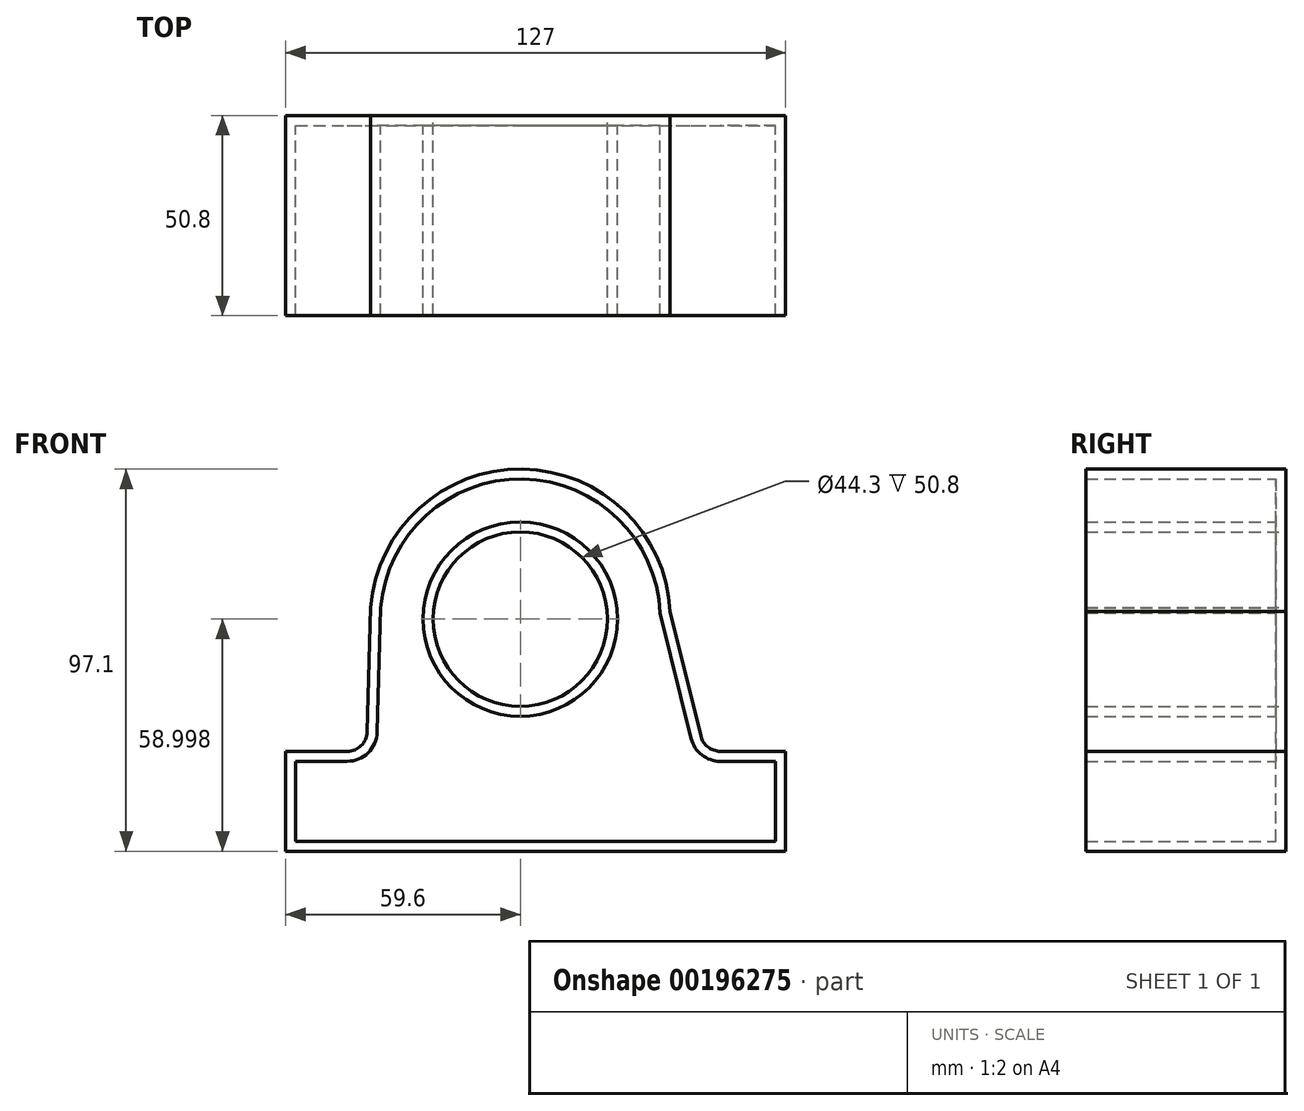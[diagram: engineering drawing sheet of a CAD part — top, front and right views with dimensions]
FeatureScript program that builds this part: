
annotation { "Feature Type Name" : "Feature", "Feature Type Description" : "" }
export const myFeature = defineFeature(function(context is Context, id is Id, definition is map)
    precondition{}
    {
        {
            var Q0;
            Q0=qCreatedBy(makeId("Front.planeOp"),FACE);
            var sketch = newSketch(context, id + "F0", { "sketchPlane" : qUnion([Q0])});
            skLineSegment(sketch, "E0", {"start": v(-59.6, -39.48) * mm, "end": v(67.4, -39.48) * mm});
            skLineSegment(sketch, "E1", {"start": v(67.4, -39.48) * mm, "end": v(67.4, -14.08) * mm});
            skLineSegment(sketch, "E2", {"start": v(67.4, -14.08) * mm, "end": v(46.84, -14.08) * mm});
            skLineSegment(sketch, "E3", {"start": v(-59.6, -39.48) * mm, "end": v(-59.6, -14.08) * mm});
            skLineSegment(sketch, "E4", {"start": v(-59.6, -14.08) * mm, "end": v(-39.04, -14.08) * mm});
            skArc(sketch, "E5", {"start": v(38.05, 21.4) * mm, "mid": v(0.53, 57.61) * mm, "end": v(-37.99, 22.46) * mm});
            skLineSegment(sketch, "E6", {"start": v(-37.99, 22.46) * mm, "end": v(-39.04, -14.08) * mm});
            skLineSegment(sketch, "E7", {"start": v(38.05, 21.4) * mm, "end": v(46.84, -14.08) * mm});
            skCircle(sketch, "E8", {"center": v(0, 19.52) * mm, "radius": 22.15 * mm});
            skSolve(sketch);
        }
        {
            var Q0;
            Q0=makeQuery(id+"F0.imprint","IMPRINT",FACE,{"disambiguationData":[TD([[makeQuery(id+"F0.imprint","IMPRINT",EDGE,{"derivedFrom":sQuery(id+"F0.wireOp",EDGE,"E0")}),1.0]])]});
            extrude(context, id + "F1", {"entities" : qUnion([Q0]), "depth" : 50.8 * mm});
        }
        {
            var Q0;
            Q0=makeQuery(id+"F1.opExtrude","SWEPT_EDGE",EDGE,{"disambiguationData":[OSD([sQuery(id+"F0.wireOp",EDGE,"E2"),sQuery(id+"F0.wireOp",EDGE,"E7")])]});
            var Q1;
            Q1=makeQuery(id+"F1.opExtrude","SWEPT_EDGE",EDGE,{"disambiguationData":[OSD([sQuery(id+"F0.wireOp",EDGE,"E4"),sQuery(id+"F0.wireOp",EDGE,"E6")])]});
            fillet(context, id + "F2", {"entities" : qUnion([Q0, Q1]), "radius" : 5.08 * mm, "tangentPropagation" : true, "allowEdgeOverflow" : false});
        }
        {
            var Q0;
            Q0=makeQuery(id+"F1.opExtrude","CAP_FACE",FACE,{"disambiguationData":[OSD([sQuery(id+"F0.wireOp",EDGE,"E0"),sQuery(id+"F0.wireOp",EDGE,"E1"),sQuery(id+"F0.wireOp",EDGE,"E2"),sQuery(id+"F0.wireOp",EDGE,"E3"),sQuery(id+"F0.wireOp",EDGE,"E4"),sQuery(id+"F0.wireOp",EDGE,"E5"),sQuery(id+"F0.wireOp",EDGE,"E6"),sQuery(id+"F0.wireOp",EDGE,"E7"),sQuery(id+"F0.wireOp",EDGE,"E8")])],"isStart":false});
            shell(context, id + "F3", {"entities" : qUnion([Q0]), "thickness" : 2.54 * mm});
        }
    });
